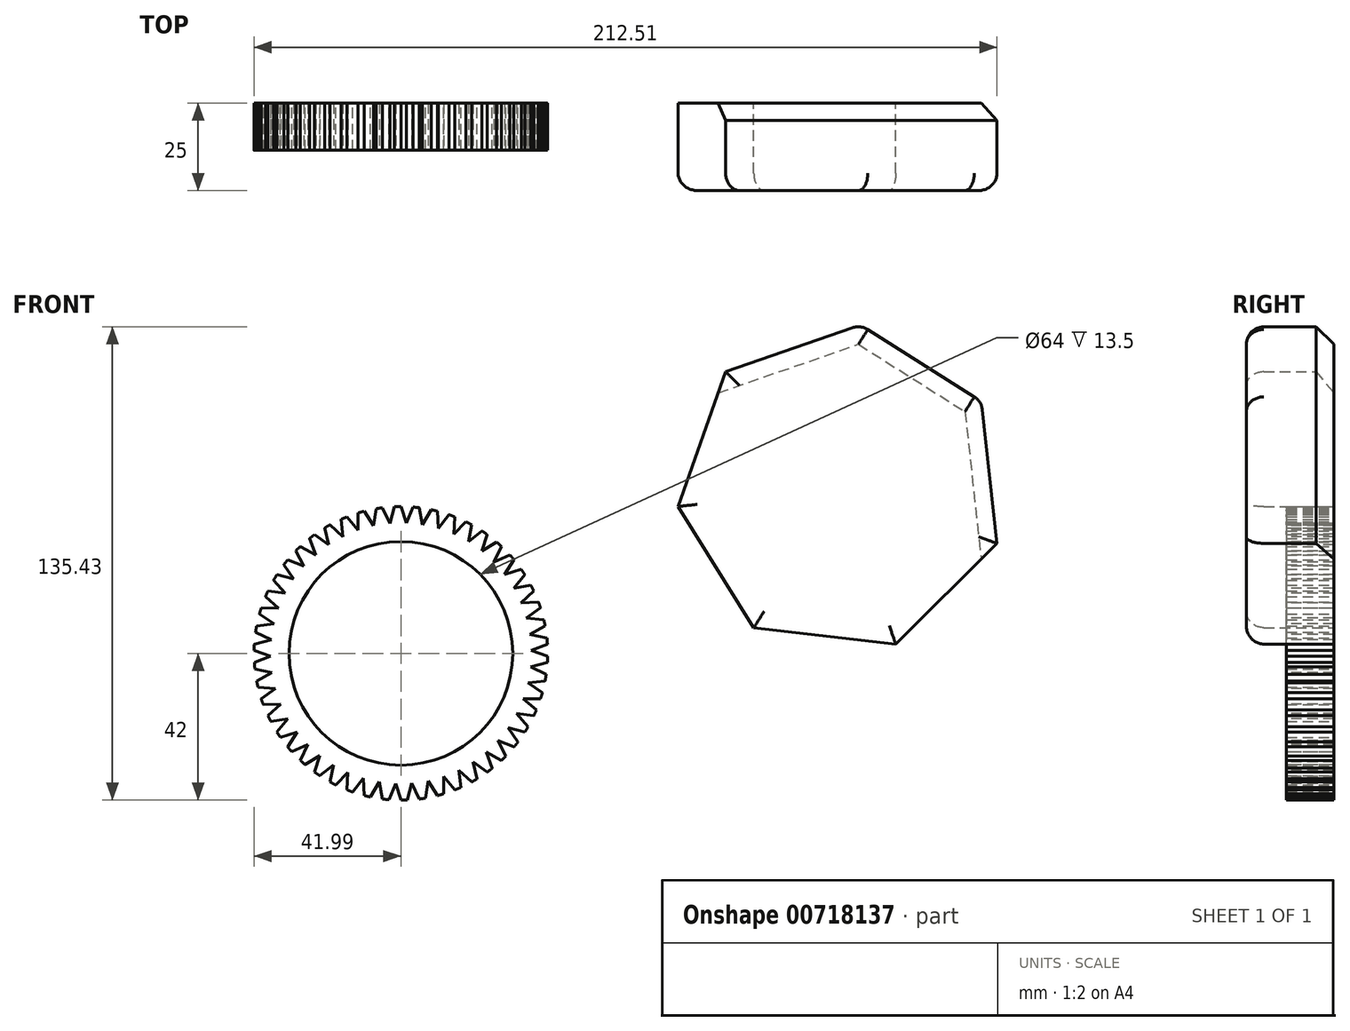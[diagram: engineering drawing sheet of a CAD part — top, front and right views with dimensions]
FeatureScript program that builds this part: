
annotation { "Feature Type Name" : "Feature", "Feature Type Description" : "" }
export const myFeature = defineFeature(function(context is Context, id is Id, definition is map)
    precondition{}
    {
        {
            var Q0;
            Q0=qCreatedBy(makeId("Front.planeOp"),FACE);
            var sketch = newSketch(context, id + "F0", { "sketchPlane" : qUnion([Q0])});
            skCircle(sketch, "E0", {"center": v(0, 0) * mm, "radius": 32 * mm});
            skCircle(sketch, "E1", {"center": v(0, 0) * mm, "radius": 42 * mm});
            skArc(sketch, "E2", {"start": v(-3.24, 36.86) * mm, "mid": v(0.8, -37) * mm, "end": v(1.63, 36.96) * mm});
            skLineSegment(sketch, "E3", {"start": v(0, 32) * mm, "end": v(0, 0) * mm});
            skLineSegment(sketch, "E4.1.0", {"start": v(1.84, 41.96) * mm, "end": v(0, 0) * mm});
            skLineSegment(sketch, "E4.2.0", {"start": v(3.69, 41.84) * mm, "end": v(0, 0) * mm});
            skLineSegment(sketch, "E4.3.0", {"start": v(5.52, 41.64) * mm, "end": v(0, 0) * mm});
            skLineSegment(sketch, "E4.4.0", {"start": v(7.34, 41.35) * mm, "end": v(0, 0) * mm});
            skLineSegment(sketch, "E4.5.0", {"start": v(9.15, 41) * mm, "end": v(0, 0) * mm});
            skLineSegment(sketch, "E4.6.0", {"start": v(10.95, 40.55) * mm, "end": v(0, 0) * mm});
            skLineSegment(sketch, "E4.7.0", {"start": v(12.72, 40.03) * mm, "end": v(0, 0) * mm});
            skLineSegment(sketch, "E4.8.0", {"start": v(14.46, 39.43) * mm, "end": v(0, 0) * mm});
            skLineSegment(sketch, "E4.9.0", {"start": v(16.18, 38.76) * mm, "end": v(0, 0) * mm});
            skLineSegment(sketch, "E4.10.0", {"start": v(17.87, 38.01) * mm, "end": v(0, 0) * mm});
            skLineSegment(sketch, "E4.11.0", {"start": v(19.52, 37.19) * mm, "end": v(0, 0) * mm});
            skLineSegment(sketch, "E4.12.0", {"start": v(21.13, 36.3) * mm, "end": v(0, 0) * mm});
            skLineSegment(sketch, "E4.13.0", {"start": v(22.7, 35.33) * mm, "end": v(0, 0) * mm});
            skLineSegment(sketch, "E4.14.0", {"start": v(24.24, 34.3) * mm, "end": v(0, 0) * mm});
            skLineSegment(sketch, "E4.15.0", {"start": v(25.72, 33.2) * mm, "end": v(0, 0) * mm});
            skLineSegment(sketch, "E4.16.0", {"start": v(27.15, 32.04) * mm, "end": v(0, 0) * mm});
            skLineSegment(sketch, "E4.17.0", {"start": v(28.54, 30.82) * mm, "end": v(0, 0) * mm});
            skLineSegment(sketch, "E4.18.0", {"start": v(29.86, 29.53) * mm, "end": v(0, 0) * mm});
            skLineSegment(sketch, "E4.19.0", {"start": v(31.13, 28.2) * mm, "end": v(0, 0) * mm});
            skLineSegment(sketch, "E4.20.0", {"start": v(32.34, 26.8) * mm, "end": v(0, 0) * mm});
            skLineSegment(sketch, "E4.21.0", {"start": v(33.49, 25.35) * mm, "end": v(0, 0) * mm});
            skLineSegment(sketch, "E4.22.0", {"start": v(34.57, 23.86) * mm, "end": v(0, 0) * mm});
            skLineSegment(sketch, "E4.23.0", {"start": v(35.58, 22.32) * mm, "end": v(0, 0) * mm});
            skLineSegment(sketch, "E4.24.0", {"start": v(36.53, 20.73) * mm, "end": v(0, 0) * mm});
            skLineSegment(sketch, "E4.25.0", {"start": v(37.4, 19.1) * mm, "end": v(0, 0) * mm});
            skLineSegment(sketch, "E4.26.0", {"start": v(38.2, 17.45) * mm, "end": v(0, 0) * mm});
            skLineSegment(sketch, "E4.27.0", {"start": v(38.93, 15.75) * mm, "end": v(0, 0) * mm});
            skLineSegment(sketch, "E4.28.0", {"start": v(39.59, 14.02) * mm, "end": v(0, 0) * mm});
            skLineSegment(sketch, "E4.29.0", {"start": v(40.17, 12.27) * mm, "end": v(0, 0) * mm});
            skLineSegment(sketch, "E4.30.0", {"start": v(40.67, 10.5) * mm, "end": v(0, 0) * mm});
            skLineSegment(sketch, "E4.31.0", {"start": v(41.09, 8.7) * mm, "end": v(0, 0) * mm});
            skLineSegment(sketch, "E4.32.0", {"start": v(41.43, 6.89) * mm, "end": v(0, 0) * mm});
            skLineSegment(sketch, "E4.33.0", {"start": v(41.7, 5.06) * mm, "end": v(0, 0) * mm});
            skLineSegment(sketch, "E4.34.0", {"start": v(41.88, 3.22) * mm, "end": v(0, 0) * mm});
            skLineSegment(sketch, "E4.35.0", {"start": v(41.98, 1.38) * mm, "end": v(0, 0) * mm});
            skLineSegment(sketch, "E4.36.0", {"start": v(42, -0.46) * mm, "end": v(0, 0) * mm});
            skLineSegment(sketch, "E4.37.0", {"start": v(41.94, -2.3) * mm, "end": v(0, 0) * mm});
            skLineSegment(sketch, "E4.38.0", {"start": v(41.8, -4.15) * mm, "end": v(0, 0) * mm});
            skLineSegment(sketch, "E4.39.0", {"start": v(41.57, -5.98) * mm, "end": v(0, 0) * mm});
            skLineSegment(sketch, "E4.40.0", {"start": v(41.27, -7.8) * mm, "end": v(0, 0) * mm});
            skLineSegment(sketch, "E4.41.0", {"start": v(40.89, -9.6) * mm, "end": v(0, 0) * mm});
            skLineSegment(sketch, "E4.42.0", {"start": v(40.43, -11.4) * mm, "end": v(0, 0) * mm});
            skLineSegment(sketch, "E4.43.0", {"start": v(39.89, -13.16) * mm, "end": v(0, 0) * mm});
            skLineSegment(sketch, "E4.44.0", {"start": v(39.27, -14.9) * mm, "end": v(0, 0) * mm});
            skLineSegment(sketch, "E4.anchor1", {"start": v(0, 0) * mm, "end": v(0, 32) * mm, "construction": true});
            skLineSegment(sketch, "E4.anchor2", {"start": v(0, 0) * mm, "end": v(-1.4, 31.97) * mm, "construction": true});
            skLineSegment(sketch, "E5.1.45.0", {"start": v(38.58, -16.6) * mm, "end": v(0, 0) * mm});
            skLineSegment(sketch, "E5.1.46.0", {"start": v(37.81, -18.29) * mm, "end": v(0, 0) * mm});
            skLineSegment(sketch, "E5.1.47.0", {"start": v(36.97, -19.93) * mm, "end": v(0, 0) * mm});
            skLineSegment(sketch, "E5.1.48.0", {"start": v(36.06, -21.53) * mm, "end": v(0, 0) * mm});
            skLineSegment(sketch, "E5.1.49.0", {"start": v(35.08, -23.1) * mm, "end": v(0, 0) * mm});
            skLineSegment(sketch, "E5.1.50.0", {"start": v(34.03, -24.62) * mm, "end": v(0, 0) * mm});
            skLineSegment(sketch, "E5.1.51.0", {"start": v(32.92, -26.09) * mm, "end": v(0, 0) * mm});
            skLineSegment(sketch, "E5.1.52.0", {"start": v(31.74, -27.5) * mm, "end": v(0, 0) * mm});
            skLineSegment(sketch, "E5.1.53.0", {"start": v(30.5, -28.88) * mm, "end": v(0, 0) * mm});
            skLineSegment(sketch, "E5.1.54.0", {"start": v(29.2, -30.19) * mm, "end": v(0, 0) * mm});
            skLineSegment(sketch, "E5.1.55.0", {"start": v(27.85, -31.44) * mm, "end": v(0, 0) * mm});
            skLineSegment(sketch, "E5.1.56.0", {"start": v(26.44, -32.63) * mm, "end": v(0, 0) * mm});
            skLineSegment(sketch, "E5.1.57.0", {"start": v(24.98, -33.76) * mm, "end": v(0, 0) * mm});
            skLineSegment(sketch, "E5.1.58.0", {"start": v(23.47, -34.83) * mm, "end": v(0, 0) * mm});
            skLineSegment(sketch, "E5.1.59.0", {"start": v(21.92, -35.83) * mm, "end": v(0, 0) * mm});
            skLineSegment(sketch, "E5.1.60.0", {"start": v(20.33, -36.75) * mm, "end": v(0, 0) * mm});
            skLineSegment(sketch, "E5.1.61.0", {"start": v(18.7, -37.61) * mm, "end": v(0, 0) * mm});
            skLineSegment(sketch, "E5.1.62.0", {"start": v(17.02, -38.4) * mm, "end": v(0, 0) * mm});
            skLineSegment(sketch, "E5.1.63.0", {"start": v(15.32, -39.1) * mm, "end": v(0, 0) * mm});
            skLineSegment(sketch, "E5.1.64.0", {"start": v(13.59, -39.74) * mm, "end": v(0, 0) * mm});
            skLineSegment(sketch, "E5.1.65.0", {"start": v(11.83, -40.3) * mm, "end": v(0, 0) * mm});
            skLineSegment(sketch, "E5.1.66.0", {"start": v(10.05, -40.78) * mm, "end": v(0, 0) * mm});
            skLineSegment(sketch, "E5.1.67.0", {"start": v(8.24, -41.18) * mm, "end": v(0, 0) * mm});
            skLineSegment(sketch, "E5.1.68.0", {"start": v(6.43, -41.5) * mm, "end": v(0, 0) * mm});
            skLineSegment(sketch, "E5.1.69.0", {"start": v(4.6, -41.75) * mm, "end": v(0, 0) * mm});
            skLineSegment(sketch, "E5.1.70.0", {"start": v(2.76, -41.9) * mm, "end": v(0, 0) * mm});
            skLineSegment(sketch, "E5.1.71.0", {"start": v(0.92, -42) * mm, "end": v(0, 0) * mm});
            skLineSegment(sketch, "E5.1.72.0", {"start": v(-0.93, -41.99) * mm, "end": v(0, 0) * mm});
            skLineSegment(sketch, "E5.1.73.0", {"start": v(-2.77, -41.9) * mm, "end": v(0, 0) * mm});
            skLineSegment(sketch, "E5.1.74.0", {"start": v(-4.61, -41.75) * mm, "end": v(0, 0) * mm});
            skLineSegment(sketch, "E5.1.75.0", {"start": v(-6.44, -41.5) * mm, "end": v(0, 0) * mm});
            skLineSegment(sketch, "E5.1.76.0", {"start": v(-8.26, -41.18) * mm, "end": v(0, 0) * mm});
            skLineSegment(sketch, "E5.1.77.0", {"start": v(-10.06, -40.78) * mm, "end": v(0, 0) * mm});
            skLineSegment(sketch, "E5.1.78.0", {"start": v(-11.84, -40.3) * mm, "end": v(0, 0) * mm});
            skLineSegment(sketch, "E5.1.79.0", {"start": v(-13.6, -39.74) * mm, "end": v(0, 0) * mm});
            skLineSegment(sketch, "E6.1.80.0", {"start": v(-15.33, -39.1) * mm, "end": v(0, 0) * mm});
            skLineSegment(sketch, "E6.1.81.0", {"start": v(-17.03, -38.4) * mm, "end": v(0, 0) * mm});
            skLineSegment(sketch, "E6.1.82.0", {"start": v(-18.7, -37.6) * mm, "end": v(0, 0) * mm});
            skLineSegment(sketch, "E6.1.83.0", {"start": v(-20.34, -36.75) * mm, "end": v(0, 0) * mm});
            skLineSegment(sketch, "E6.1.84.0", {"start": v(-21.93, -35.82) * mm, "end": v(0, 0) * mm});
            skLineSegment(sketch, "E6.1.85.0", {"start": v(-23.48, -34.82) * mm, "end": v(0, 0) * mm});
            skLineSegment(sketch, "E6.1.86.0", {"start": v(-25, -33.76) * mm, "end": v(0, 0) * mm});
            skLineSegment(sketch, "E6.1.87.0", {"start": v(-26.45, -32.63) * mm, "end": v(0, 0) * mm});
            skLineSegment(sketch, "E6.1.88.0", {"start": v(-27.86, -31.43) * mm, "end": v(0, 0) * mm});
            skLineSegment(sketch, "E6.1.89.0", {"start": v(-29.21, -30.18) * mm, "end": v(0, 0) * mm});
            skLineSegment(sketch, "E7.1.90.0", {"start": v(-30.5, -28.87) * mm, "end": v(0, 0) * mm});
            skLineSegment(sketch, "E7.1.91.0", {"start": v(-31.75, -27.5) * mm, "end": v(0, 0) * mm});
            skLineSegment(sketch, "E7.1.92.0", {"start": v(-32.92, -26.08) * mm, "end": v(0, 0) * mm});
            skLineSegment(sketch, "E7.1.93.0", {"start": v(-34.04, -24.6) * mm, "end": v(0, 0) * mm});
            skLineSegment(sketch, "E7.1.94.0", {"start": v(-35.09, -23.09) * mm, "end": v(0, 0) * mm});
            skLineSegment(sketch, "E7.1.95.0", {"start": v(-36.07, -21.52) * mm, "end": v(0, 0) * mm});
            skLineSegment(sketch, "E7.1.96.0", {"start": v(-36.98, -19.92) * mm, "end": v(0, 0) * mm});
            skLineSegment(sketch, "E7.1.97.0", {"start": v(-37.82, -18.27) * mm, "end": v(0, 0) * mm});
            skLineSegment(sketch, "E7.1.98.0", {"start": v(-38.58, -16.6) * mm, "end": v(0, 0) * mm});
            skLineSegment(sketch, "E7.1.99.0", {"start": v(-39.27, -14.89) * mm, "end": v(0, 0) * mm});
            skLineSegment(sketch, "E7.1.100.0", {"start": v(-39.89, -13.15) * mm, "end": v(0, 0) * mm});
            skLineSegment(sketch, "E7.1.101.0", {"start": v(-40.43, -11.38) * mm, "end": v(0, 0) * mm});
            skLineSegment(sketch, "E7.1.102.0", {"start": v(-40.89, -9.6) * mm, "end": v(0, 0) * mm});
            skLineSegment(sketch, "E7.1.103.0", {"start": v(-41.27, -7.79) * mm, "end": v(0, 0) * mm});
            skLineSegment(sketch, "E7.1.104.0", {"start": v(-41.57, -5.97) * mm, "end": v(0, 0) * mm});
            skLineSegment(sketch, "E7.1.105.0", {"start": v(-41.8, -4.14) * mm, "end": v(0, 0) * mm});
            skLineSegment(sketch, "E7.1.106.0", {"start": v(-41.94, -2.3) * mm, "end": v(0, 0) * mm});
            skLineSegment(sketch, "E7.1.107.0", {"start": v(-42, -0.45) * mm, "end": v(0, 0) * mm});
            skLineSegment(sketch, "E7.1.108.0", {"start": v(-41.98, 1.4) * mm, "end": v(0, 0) * mm});
            skLineSegment(sketch, "E7.1.109.0", {"start": v(-41.88, 3.24) * mm, "end": v(0, 0) * mm});
            skLineSegment(sketch, "E7.1.110.0", {"start": v(-41.7, 5.07) * mm, "end": v(0, 0) * mm});
            skLineSegment(sketch, "E7.1.111.0", {"start": v(-41.43, 6.9) * mm, "end": v(0, 0) * mm});
            skLineSegment(sketch, "E7.1.112.0", {"start": v(-41.09, 8.71) * mm, "end": v(0, 0) * mm});
            skLineSegment(sketch, "E7.1.113.0", {"start": v(-40.66, 10.5) * mm, "end": v(0, 0) * mm});
            skLineSegment(sketch, "E7.1.114.0", {"start": v(-40.16, 12.28) * mm, "end": v(0, 0) * mm});
            skLineSegment(sketch, "E7.1.115.0", {"start": v(-39.58, 14.04) * mm, "end": v(0, 0) * mm});
            skLineSegment(sketch, "E7.1.116.0", {"start": v(-38.93, 15.76) * mm, "end": v(0, 0) * mm});
            skLineSegment(sketch, "E7.1.117.0", {"start": v(-38.2, 17.46) * mm, "end": v(0, 0) * mm});
            skLineSegment(sketch, "E7.1.118.0", {"start": v(-37.4, 19.12) * mm, "end": v(0, 0) * mm});
            skLineSegment(sketch, "E7.1.119.0", {"start": v(-36.52, 20.74) * mm, "end": v(0, 0) * mm});
            skLineSegment(sketch, "E8.1.120.0", {"start": v(-35.57, 22.33) * mm, "end": v(0, 0) * mm});
            skLineSegment(sketch, "E8.1.121.0", {"start": v(-34.56, 23.87) * mm, "end": v(0, 0) * mm});
            skLineSegment(sketch, "E8.1.122.0", {"start": v(-33.48, 25.36) * mm, "end": v(0, 0) * mm});
            skLineSegment(sketch, "E8.1.123.0", {"start": v(-32.33, 26.8) * mm, "end": v(0, 0) * mm});
            skLineSegment(sketch, "E9.1.124.0", {"start": v(-31.12, 28.2) * mm, "end": v(0, 0) * mm});
            skLineSegment(sketch, "E9.1.125.0", {"start": v(-29.85, 29.54) * mm, "end": v(0, 0) * mm});
            skLineSegment(sketch, "E9.1.126.0", {"start": v(-28.53, 30.83) * mm, "end": v(0, 0) * mm});
            skLineSegment(sketch, "E9.1.127.0", {"start": v(-27.15, 32.05) * mm, "end": v(0, 0) * mm});
            skLineSegment(sketch, "E9.1.128.0", {"start": v(-25.71, 33.21) * mm, "end": v(0, 0) * mm});
            skLineSegment(sketch, "E9.1.129.0", {"start": v(-24.23, 34.3) * mm, "end": v(0, 0) * mm});
            skLineSegment(sketch, "E9.1.130.0", {"start": v(-22.7, 35.34) * mm, "end": v(0, 0) * mm});
            skLineSegment(sketch, "E9.1.131.0", {"start": v(-21.12, 36.3) * mm, "end": v(0, 0) * mm});
            skLineSegment(sketch, "E9.1.132.0", {"start": v(-19.5, 37.2) * mm, "end": v(0, 0) * mm});
            skLineSegment(sketch, "E9.1.133.0", {"start": v(-17.86, 38.02) * mm, "end": v(0, 0) * mm});
            skLineSegment(sketch, "E9.1.134.0", {"start": v(-16.17, 38.76) * mm, "end": v(0, 0) * mm});
            skLineSegment(sketch, "E10.1.135.0", {"start": v(-14.45, 39.44) * mm, "end": v(0, 0) * mm});
            skLineSegment(sketch, "E11.1.136.0", {"start": v(-12.7, 40.03) * mm, "end": v(0, 0) * mm});
            skLineSegment(sketch, "E11.1.137.0", {"start": v(-10.93, 40.55) * mm, "end": v(0, 0) * mm});
            skLineSegment(sketch, "E11.1.138.0", {"start": v(-9.14, 41) * mm, "end": v(0, 0) * mm});
            skLineSegment(sketch, "E11.1.139.0", {"start": v(-7.33, 41.36) * mm, "end": v(0, 0) * mm});
            skLineSegment(sketch, "E11.1.140.0", {"start": v(-5.5, 41.64) * mm, "end": v(0, 0) * mm});
            skLineSegment(sketch, "E11.1.141.0", {"start": v(-3.67, 41.84) * mm, "end": v(0, 0) * mm});
            skLineSegment(sketch, "E11.1.142.0", {"start": v(-1.4, 31.97) * mm, "end": v(0, 0) * mm});
            skLineSegment(sketch, "E12", {"start": v(-1.83, 41.96) * mm, "end": v(-3.24, 36.86) * mm});
            skLineSegment(sketch, "E13", {"start": v(0, 42) * mm, "end": v(1.63, 36.96) * mm});
            skSolve(sketch);
        }
        {
            var Q0;
            Q0=qCreatedBy(makeId("Top.planeOp"),FACE);
            var sketch = newSketch(context, id + "F1", { "sketchPlane" : qUnion([Q0])});
            skLineSegment(sketch, "E14", {"start": v(0, 0) * mm, "end": v(0, -22.9) * mm});
            skSolve(sketch);
        }
        {
            var Q0;
            {var subQ0=sQuery(id+"F0.wireOp",EDGE,"E12");Q0=makeQuery(id+"F0.imprint","IMPRINT",FACE,{"disambiguationData":[TD([[makeQuery(id+"F0.imprint","IMPRINT",EDGE,{"derivedFrom":subQ0}),1.0]])]});}
            extrude(context, id + "F2", {"entities" : qUnion([Q0]), "depth" : 13.5 * mm, "offsetDistance" : 25 * mm});
        }
        {
            var Q0;
            Q0=makeQuery(id+"F2.opExtrude","SWEPT_BODY",BODY,{"disambiguationData":[OSD([sQuery(id+"F0.wireOp",EDGE,"E0"),sQuery(id+"F0.wireOp",EDGE,"E1"),sQuery(id+"F0.wireOp",EDGE,"E4.1.0"),sQuery(id+"F0.wireOp",EDGE,"E11.1.141.0"),sQuery(id+"F0.wireOp",EDGE,"E12"),sQuery(id+"F0.wireOp",EDGE,"E13")])]});
            var Q1;
            Q1=sQuery(id+"F1.wireOp",EDGE,"E14");
            circularPattern(context, id + "F3", {"operationType" : NewBodyOperationType.ADD, "entities" : qUnion([Q0]), "axis" : qUnion([Q1]), "angle" : 360 * degree, "instanceCount" : 50, "equalSpace" : true});
        }
        {
            var Q0;
            Q0=qCreatedBy(makeId("Front.planeOp"),FACE);
            var sketch = newSketch(context, id + "F4", { "sketchPlane" : qUnion([Q0])});
            skCircle(sketch, "E15.cCircle", {"center": v(126.11, 47.16) * mm, "radius": 42.43 * mm, "construction": true});
            skLineSegment(sketch, "E15.0", {"start": v(170.52, 31.48) * mm, "end": v(141.54, 2.66) * mm});
            skLineSegment(sketch, "E15.1", {"start": v(141.54, 2.66) * mm, "end": v(100.94, 7.36) * mm});
            skLineSegment(sketch, "E15.2", {"start": v(100.94, 7.36) * mm, "end": v(79.3, 42.02) * mm});
            skLineSegment(sketch, "E15.3", {"start": v(79.3, 42.02) * mm, "end": v(92.9, 80.56) * mm});
            skLineSegment(sketch, "E15.4", {"start": v(92.9, 80.56) * mm, "end": v(131.52, 93.95) * mm});
            skLineSegment(sketch, "E15.5", {"start": v(131.52, 93.95) * mm, "end": v(166.06, 72.1) * mm});
            skLineSegment(sketch, "E15.6", {"start": v(166.06, 72.1) * mm, "end": v(170.52, 31.48) * mm});
            skPoint(sketch, "E15.0.midPoint", {"position": v(156.03, 17.07) * mm});
            skSolve(sketch);
        }
        {
            var Q0;
            Q0=makeQuery(id+"F4.imprint","IMPRINT",FACE,{"disambiguationData":[TD([[makeQuery(id+"F4.imprint","IMPRINT",EDGE,{"derivedFrom":sQuery(id+"F4.wireOp",EDGE,"E15.0")}),-1.0]])]});
            extrude(context, id + "F5", {"entities" : qUnion([Q0]), "depth" : 25 * mm, "offsetDistance" : 25 * mm});
        }
        {
            var Q0;
            Q0=makeQuery(id+"F5.opExtrude","CAP_EDGE",EDGE,{"disambiguationData":[OSD([sQuery(id+"F4.wireOp",EDGE,"E15.5")])],"isStart":false});
            fillet(context, id + "F6", {"entities" : qUnion([Q0]), "radius" : 5 * mm, "tangentPropagation" : true, "allowEdgeOverflow" : false});
        }
        {
            var Q0;
            Q0=makeQuery(id+"F5.opExtrude","CAP_EDGE",EDGE,{"disambiguationData":[OSD([sQuery(id+"F4.wireOp",EDGE,"E15.6")])],"isStart":false});
            var Q1;
            Q1=makeQuery(id+"F5.opExtrude","CAP_EDGE",EDGE,{"disambiguationData":[OSD([sQuery(id+"F4.wireOp",EDGE,"E15.0")])],"isStart":false});
            var Q2;
            Q2=makeQuery(id+"F5.opExtrude","CAP_EDGE",EDGE,{"disambiguationData":[OSD([sQuery(id+"F4.wireOp",EDGE,"E15.1")])],"isStart":false});
            var Q3;
            Q3=makeQuery(id+"F5.opExtrude","CAP_EDGE",EDGE,{"disambiguationData":[OSD([sQuery(id+"F4.wireOp",EDGE,"E15.2")])],"isStart":false});
            var Q4;
            Q4=makeQuery(id+"F5.opExtrude","CAP_EDGE",EDGE,{"disambiguationData":[OSD([sQuery(id+"F4.wireOp",EDGE,"E15.3")])],"isStart":false});
            var Q5;
            Q5=makeQuery(id+"F5.opExtrude","CAP_EDGE",EDGE,{"disambiguationData":[OSD([sQuery(id+"F4.wireOp",EDGE,"E15.4")])],"isStart":false});
            fillet(context, id + "F7", {"entities" : qUnion([Q0, Q1, Q2, Q3, Q4, Q5]), "radius" : 5 * mm, "tangentPropagation" : true, "allowEdgeOverflow" : false});
        }
        {
            var Q0;
            Q0=makeQuery(id+"F5.opExtrude","CAP_EDGE",EDGE,{"disambiguationData":[OSD([sQuery(id+"F4.wireOp",EDGE,"E15.4")])],"isStart":true});
            chamfer(context, id + "F8", {"entities" : qUnion([Q0]), "width" : 5 * mm, "tangentPropagation" : true});
        }
    });
